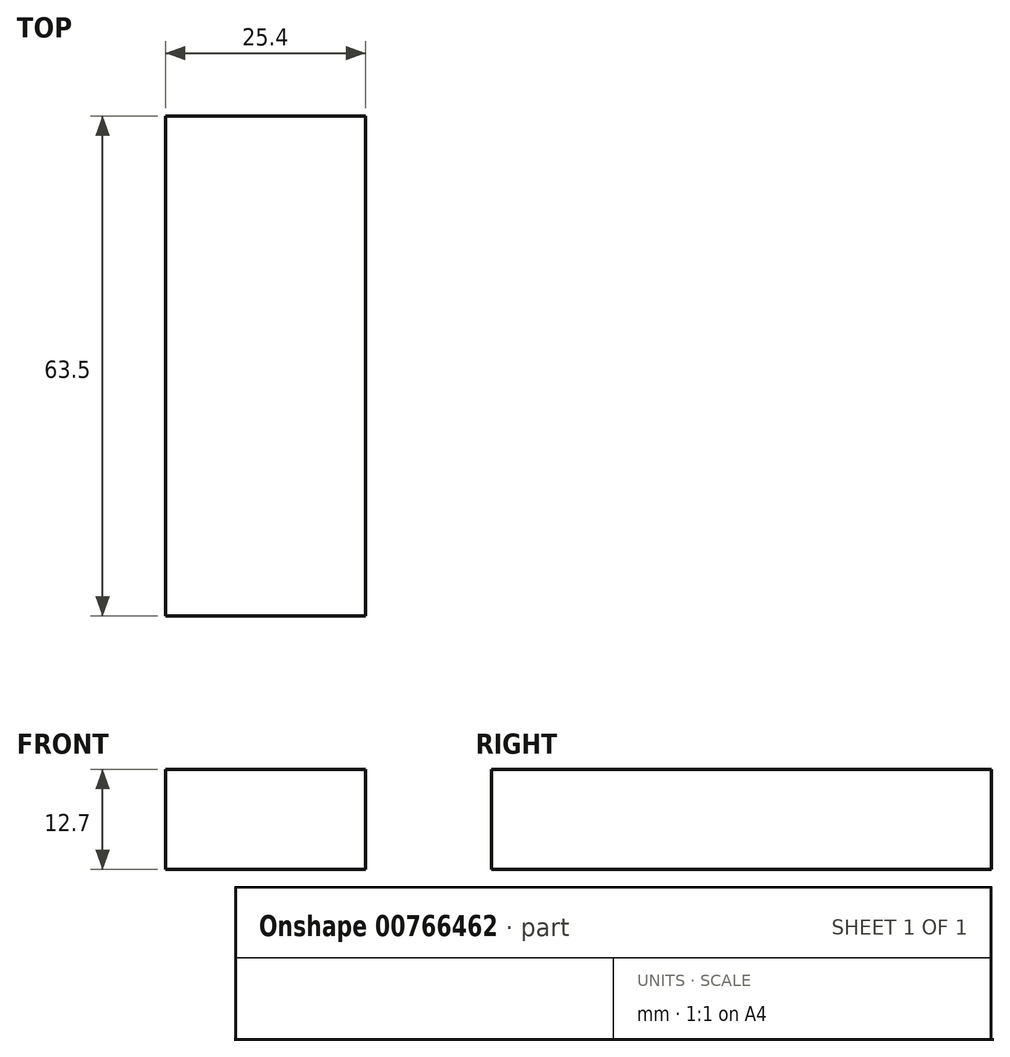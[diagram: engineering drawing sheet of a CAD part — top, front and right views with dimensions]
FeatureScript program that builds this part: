
annotation { "Feature Type Name" : "Feature", "Feature Type Description" : "" }
export const myFeature = defineFeature(function(context is Context, id is Id, definition is map)
    precondition{}
    {
        {
            var Q0;
            Q0=qCreatedBy(makeId("Front.planeOp"),FACE);
            var sketch = newSketch(context, id + "F0", { "sketchPlane" : qUnion([Q0])});
            skLineSegment(sketch, "E0.bottom", {"start": v(57.27, 45.08) * mm, "end": v(31.87, 45.08) * mm});
            skLineSegment(sketch, "E0.top", {"start": v(57.27, 32.38) * mm, "end": v(31.87, 32.38) * mm});
            skLineSegment(sketch, "E0.left", {"start": v(57.27, 45.08) * mm, "end": v(57.27, 32.38) * mm});
            skLineSegment(sketch, "E0.right", {"start": v(31.87, 45.08) * mm, "end": v(31.87, 32.38) * mm});
            skSolve(sketch);
        }
        {
            var Q0;
            Q0 = qSketchRegion(id + "F0", true);
            extrude(context, id + "F1", {"entities" : qUnion([Q0]), "depth" : 63.5 * mm, "offsetDistance" : 25.4 * mm});
        }
    });
